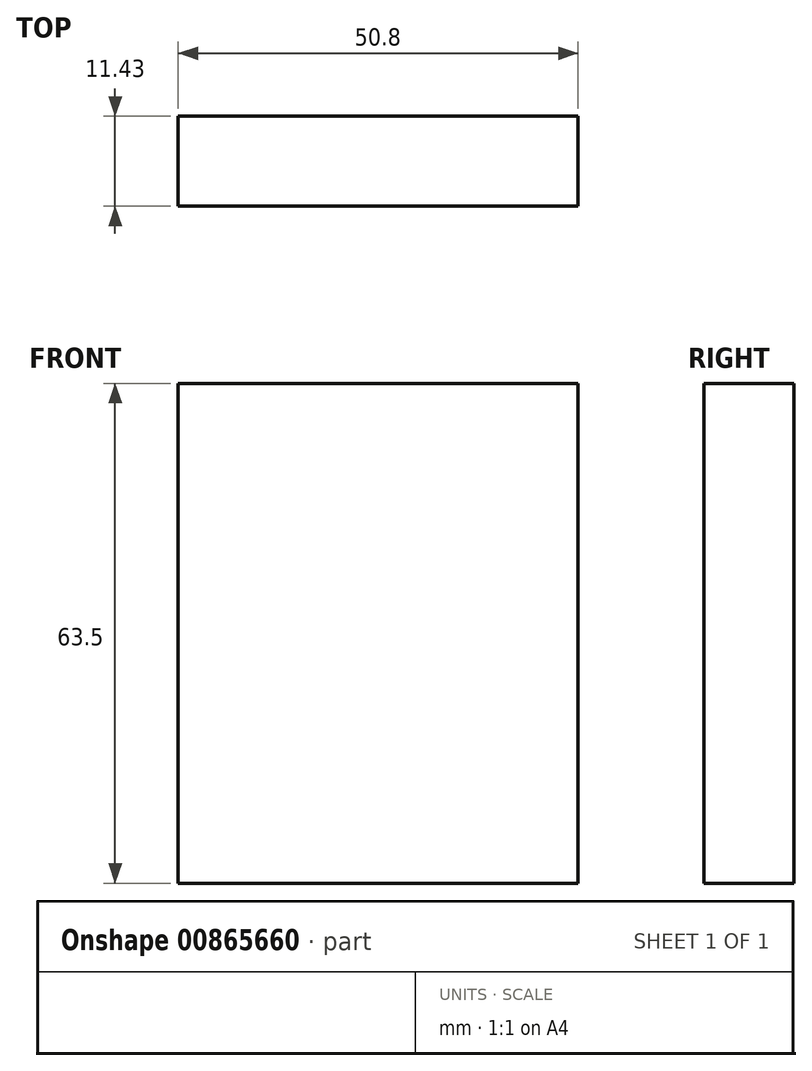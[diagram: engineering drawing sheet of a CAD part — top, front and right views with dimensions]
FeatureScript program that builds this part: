
annotation { "Feature Type Name" : "Feature", "Feature Type Description" : "" }
export const myFeature = defineFeature(function(context is Context, id is Id, definition is map)
    precondition{}
    {
        {
            var Q0;
            Q0=qCreatedBy(makeId("Front.planeOp"),FACE);
            var sketch = newSketch(context, id + "F0", { "sketchPlane" : qUnion([Q0])});
            skLineSegment(sketch, "E0.bottom", {"start": v(46.21, 35.72) * mm, "end": v(-4.59, 35.72) * mm});
            skLineSegment(sketch, "E0.top", {"start": v(46.21, -27.78) * mm, "end": v(-4.59, -27.78) * mm});
            skLineSegment(sketch, "E0.left", {"start": v(46.21, 35.72) * mm, "end": v(46.21, -27.78) * mm});
            skLineSegment(sketch, "E0.right", {"start": v(-4.59, 35.72) * mm, "end": v(-4.59, -27.78) * mm});
            skSolve(sketch);
        }
        {
            var Q0;
            Q0=makeQuery(id+"F0.imprint","IMPRINT",FACE,{"disambiguationData":[TD([[makeQuery(id+"F0.imprint","IMPRINT",EDGE,{"derivedFrom":sQuery(id+"F0.wireOp",EDGE,"E0.bottom")}),1.0]])]});
            extrude(context, id + "F1", {"entities" : qUnion([Q0]), "depth" : 11.43 * mm, "offsetDistance" : 25.4 * mm});
        }
    });
